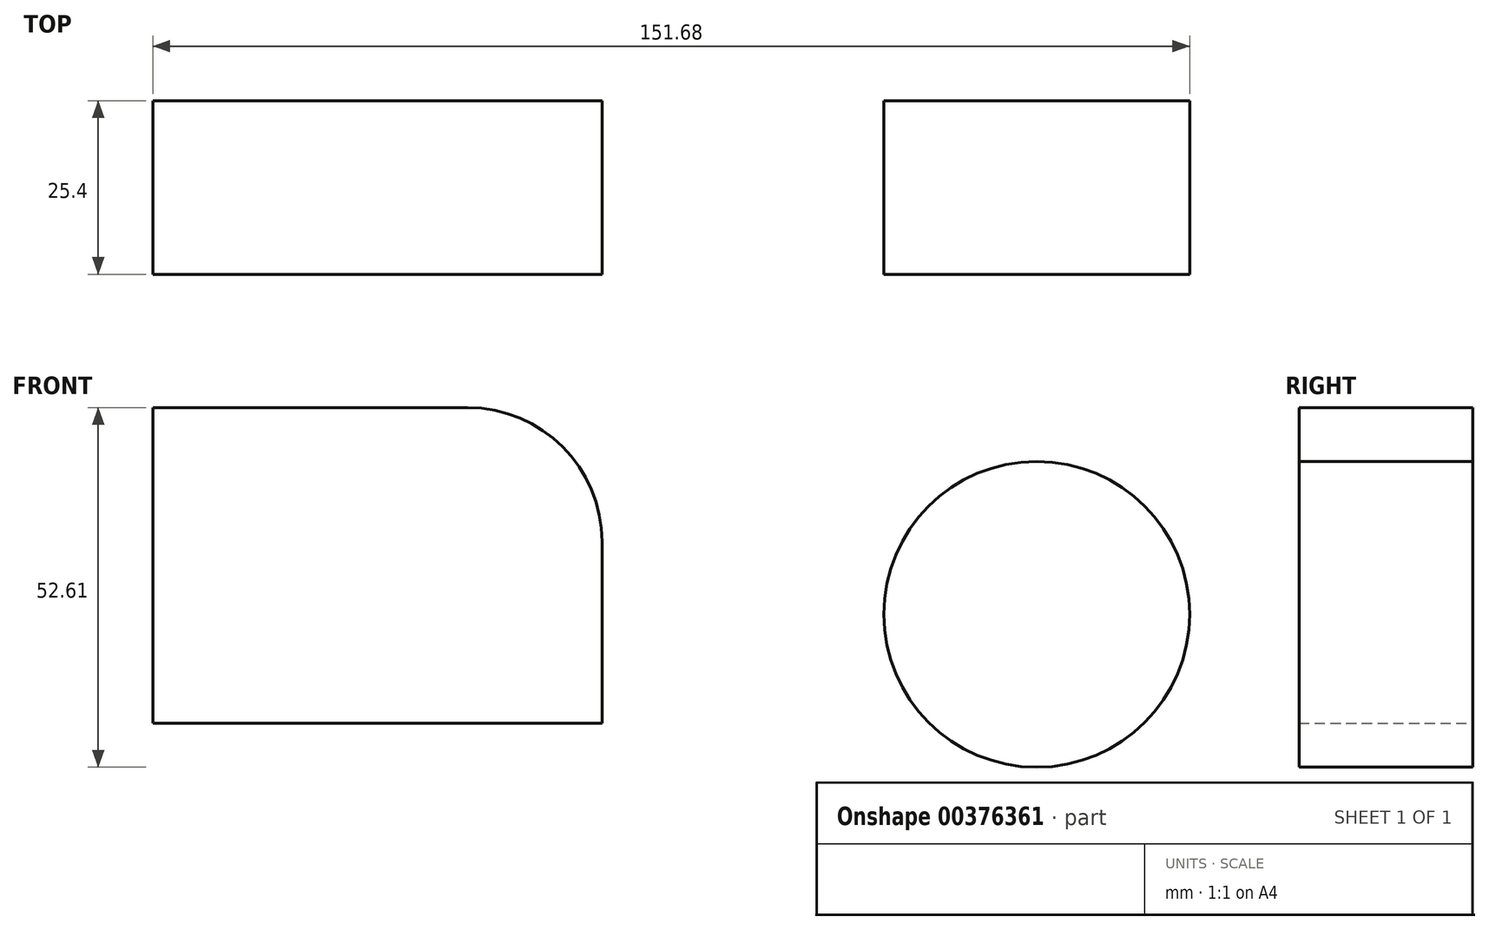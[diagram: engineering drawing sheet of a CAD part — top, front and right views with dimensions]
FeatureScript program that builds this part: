
annotation { "Feature Type Name" : "Feature", "Feature Type Description" : "" }
export const myFeature = defineFeature(function(context is Context, id is Id, definition is map)
    precondition{}
    {
        {
            var Q0;
            Q0=qCreatedBy(makeId("Front.planeOp"),FACE);
            var sketch = newSketch(context, id + "F0", { "sketchPlane" : qUnion([Q0])});
            skLineSegment(sketch, "E0.bottom", {"start": v(-124.92, 72.26) * mm, "end": v(-59.22, 72.26) * mm});
            skLineSegment(sketch, "E0.top", {"start": v(-124.92, 26.12) * mm, "end": v(-59.22, 26.12) * mm});
            skLineSegment(sketch, "E0.left", {"start": v(-124.92, 72.26) * mm, "end": v(-124.92, 26.12) * mm});
            skLineSegment(sketch, "E0.right", {"start": v(-59.22, 72.26) * mm, "end": v(-59.22, 26.12) * mm});
            skCircle(sketch, "E1", {"center": v(4.4, 42.02) * mm, "radius": 22.37 * mm});
            skSolve(sketch);
        }
        {
            var Q0;
            Q0 = qSketchRegion(id + "F0", true);
            extrude(context, id + "F1", {"entities" : qUnion([Q0]), "depth" : 25.4 * mm});
        }
        {
            var Q0;
            Q0=makeQuery(id+"F1.opExtrude","SWEPT_EDGE",EDGE,{"disambiguationData":[OSD([sQuery(id+"F0.wireOp",EDGE,"E0.bottom"),sQuery(id+"F0.wireOp",EDGE,"E0.right")])]});
            fillet(context, id + "F2", {"entities" : qUnion([Q0]), "radius" : 19.62 * mm, "tangentPropagation" : true, "allowEdgeOverflow" : false});
        }
    });
